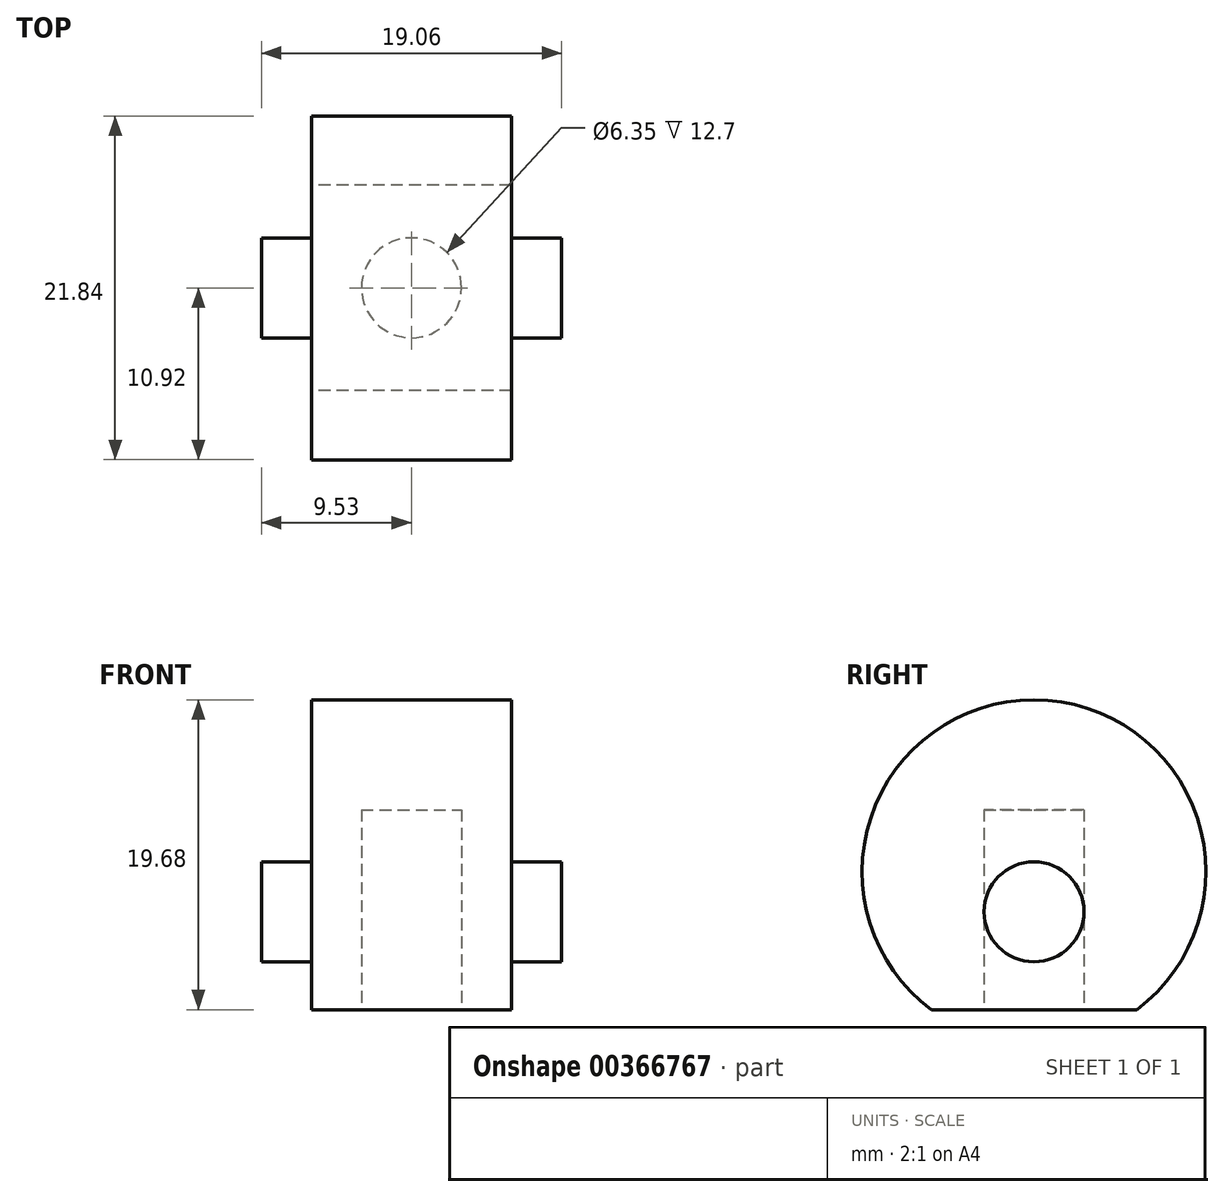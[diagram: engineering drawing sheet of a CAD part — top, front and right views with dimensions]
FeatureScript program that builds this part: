
annotation { "Feature Type Name" : "Feature", "Feature Type Description" : "" }
export const myFeature = defineFeature(function(context is Context, id is Id, definition is map)
    precondition{}
    {
        {
            var Q0;
            Q0=qCreatedBy(makeId("Right.planeOp"),FACE);
            var sketch = newSketch(context, id + "F0", { "sketchPlane" : qUnion([Q0])});
            skArc(sketch, "E0", {"start": v(6.52, -6.22) * mm, "mid": v(0, 13.46) * mm, "end": v(-6.52, -6.22) * mm});
            skLineSegment(sketch, "E1", {"start": v(6.52, -6.22) * mm, "end": v(-6.52, -6.22) * mm});
            skSolve(sketch);
        }
        {
            var Q0;
            Q0=makeQuery(id+"F0.imprint","IMPRINT",FACE,{"disambiguationData":[TD([[makeQuery(id+"F0.imprint","IMPRINT",EDGE,{"derivedFrom":sQuery(id+"F0.wireOp",EDGE,"E0")}),1.0]])]});
            extrude(context, id + "F1", {"entities" : qUnion([Q0]), "endBound" : BoundingType.SYMMETRIC, "depth" : 12.7 * mm});
        }
        {
            var Q0;
            Q0=qCreatedBy(makeId("Right.planeOp"),FACE);
            var sketch = newSketch(context, id + "F2", { "sketchPlane" : qUnion([Q0])});
            skCircle(sketch, "E2", {"center": v(0, 0) * mm, "radius": 3.18 * mm});
            skSolve(sketch);
        }
        {
            var Q0;
            Q0 = qSketchRegion(id + "F2", true);
            extrude(context, id + "F3", {"entities" : qUnion([Q0]), "endBound" : BoundingType.SYMMETRIC, "depth" : 19.05 * mm});
        }
        {
            var Q0;
            Q0=qCreatedBy(makeId("Right.planeOp"),FACE);
            var sketch = newSketch(context, id + "F4", { "sketchPlane" : qUnion([Q0])});
            skCircle(sketch, "E3", {"center": v(0, 0) * mm, "radius": 3.18 * mm});
            skSolve(sketch);
        }
        {
            var Q0;
            Q0 = qSketchRegion(id + "F4", true);
            extrude(context, id + "F5", {"entities" : qUnion([Q0]), "operationType" : NewBodyOperationType.ADD, "endBound" : BoundingType.SYMMETRIC, "depth" : 19.05 * mm});
        }
        {
            var Q0;
            Q0=makeQuery(id+"F1.opExtrude","SWEPT_FACE",FACE,{"disambiguationData":[OSD([sQuery(id+"F0.wireOp",EDGE,"E1")])]});
            var sketch = newSketch(context, id + "F6", { "sketchPlane" : qUnion([Q0])});
            skCircle(sketch, "E4", {"center": v(0, 0) * mm, "radius": 3.18 * mm});
            skSolve(sketch);
        }
        {
            var Q0;
            Q0 = qSketchRegion(id + "F6", true);
            extrude(context, id + "F7", {"entities" : qUnion([Q0]), "operationType" : NewBodyOperationType.REMOVE, "oppositeDirection" : true, "depth" : 12.7 * mm});
        }
    });
